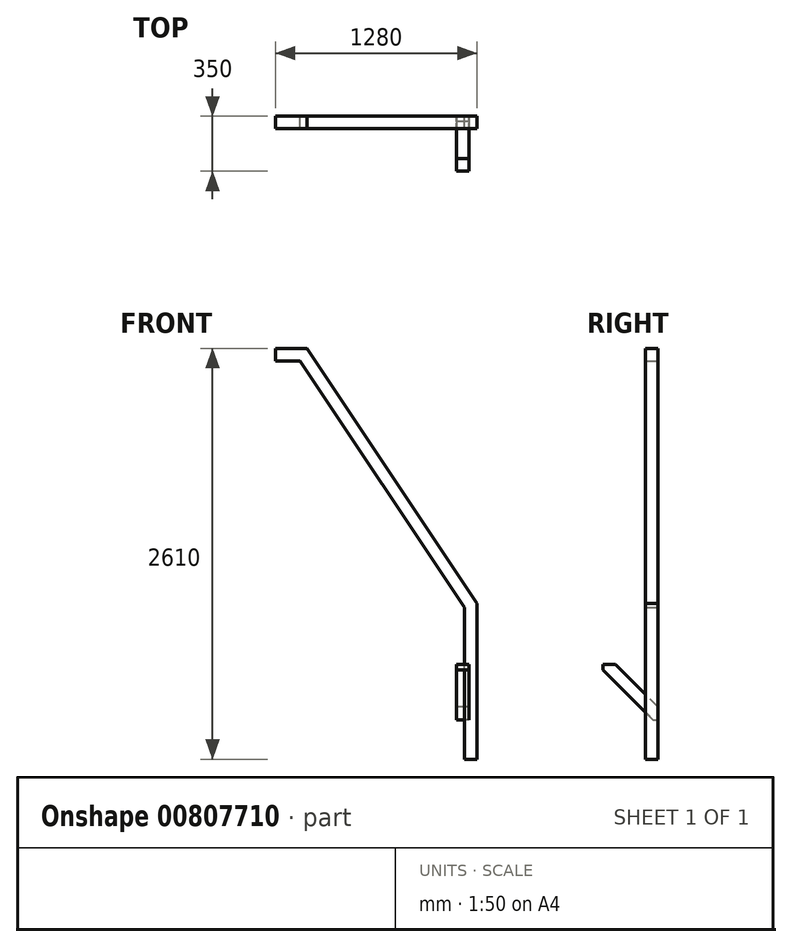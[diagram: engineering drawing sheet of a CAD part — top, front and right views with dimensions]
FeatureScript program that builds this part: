
annotation { "Feature Type Name" : "Feature", "Feature Type Description" : "" }
export const myFeature = defineFeature(function(context is Context, id is Id, definition is map)
    precondition{}
    {
        {
            var Q0;
            Q0=qCreatedBy(makeId("Right.planeOp"),FACE);
            var sketch = newSketch(context, id + "F0", { "sketchPlane" : qUnion([Q0])});
            skLineSegment(sketch, "E0", {"start": v(0, 0) * mm, "end": v(0, 80) * mm});
            skLineSegment(sketch, "E1", {"start": v(0, 80) * mm, "end": v(-270, 350) * mm});
            skLineSegment(sketch, "E2", {"start": v(-270, 350) * mm, "end": v(-350, 350) * mm});
            skLineSegment(sketch, "E3", {"start": v(-350, 316.86) * mm, "end": v(-33.14, 0) * mm});
            skLineSegment(sketch, "E4", {"start": v(-33.14, 0) * mm, "end": v(0, 0) * mm});
            skLineSegment(sketch, "E5", {"start": v(-350, 350) * mm, "end": v(-350, 316.86) * mm});
            skSolve(sketch);
        }
        {
            var Q0;
            Q0=makeQuery(id+"F0.imprint","IMPRINT",FACE,{"disambiguationData":[TD([[makeQuery(id+"F0.imprint","IMPRINT",EDGE,{"derivedFrom":sQuery(id+"F0.wireOp",EDGE,"E0")}),1.0]])]});
            extrude(context, id + "F1", {"entities" : qUnion([Q0]), "depth" : 80 * mm, "offsetDistance" : 25 * mm});
        }
        {
            var Q0;
            Q0=qCreatedBy(makeId("Front.planeOp"),FACE);
            var sketch = newSketch(context, id + "F2", { "sketchPlane" : qUnion([Q0])});
            skLineSegment(sketch, "E6", {"start": v(-991.68, 2278.3) * mm, "end": v(51.14, 714.08) * mm});
            skLineSegment(sketch, "E7", {"start": v(-948.86, 2358.3) * mm, "end": v(131.14, 738.3) * mm});
            skLineSegment(sketch, "E8", {"start": v(-948.86, 2358.3) * mm, "end": v(-1148.86, 2358.3) * mm});
            skLineSegment(sketch, "E9", {"start": v(-1148.86, 2358.3) * mm, "end": v(-1148.86, 2278.3) * mm});
            skLineSegment(sketch, "E10", {"start": v(-1148.86, 2278.3) * mm, "end": v(-991.68, 2278.3) * mm});
            skLineSegment(sketch, "E11", {"start": v(131.14, -251.7) * mm, "end": v(131.14, 738.3) * mm});
            skLineSegment(sketch, "E12", {"start": v(131.14, -251.7) * mm, "end": v(51.14, -251.7) * mm});
            skLineSegment(sketch, "E13", {"start": v(51.14, -251.7) * mm, "end": v(51.14, 714.08) * mm});
            skSolve(sketch);
        }
        {
            var Q0;
            Q0 = qSketchRegion(id + "F2", true);
            extrude(context, id + "F3", {"entities" : qUnion([Q0]), "depth" : 80 * mm, "offsetDistance" : 25 * mm});
        }
    });
